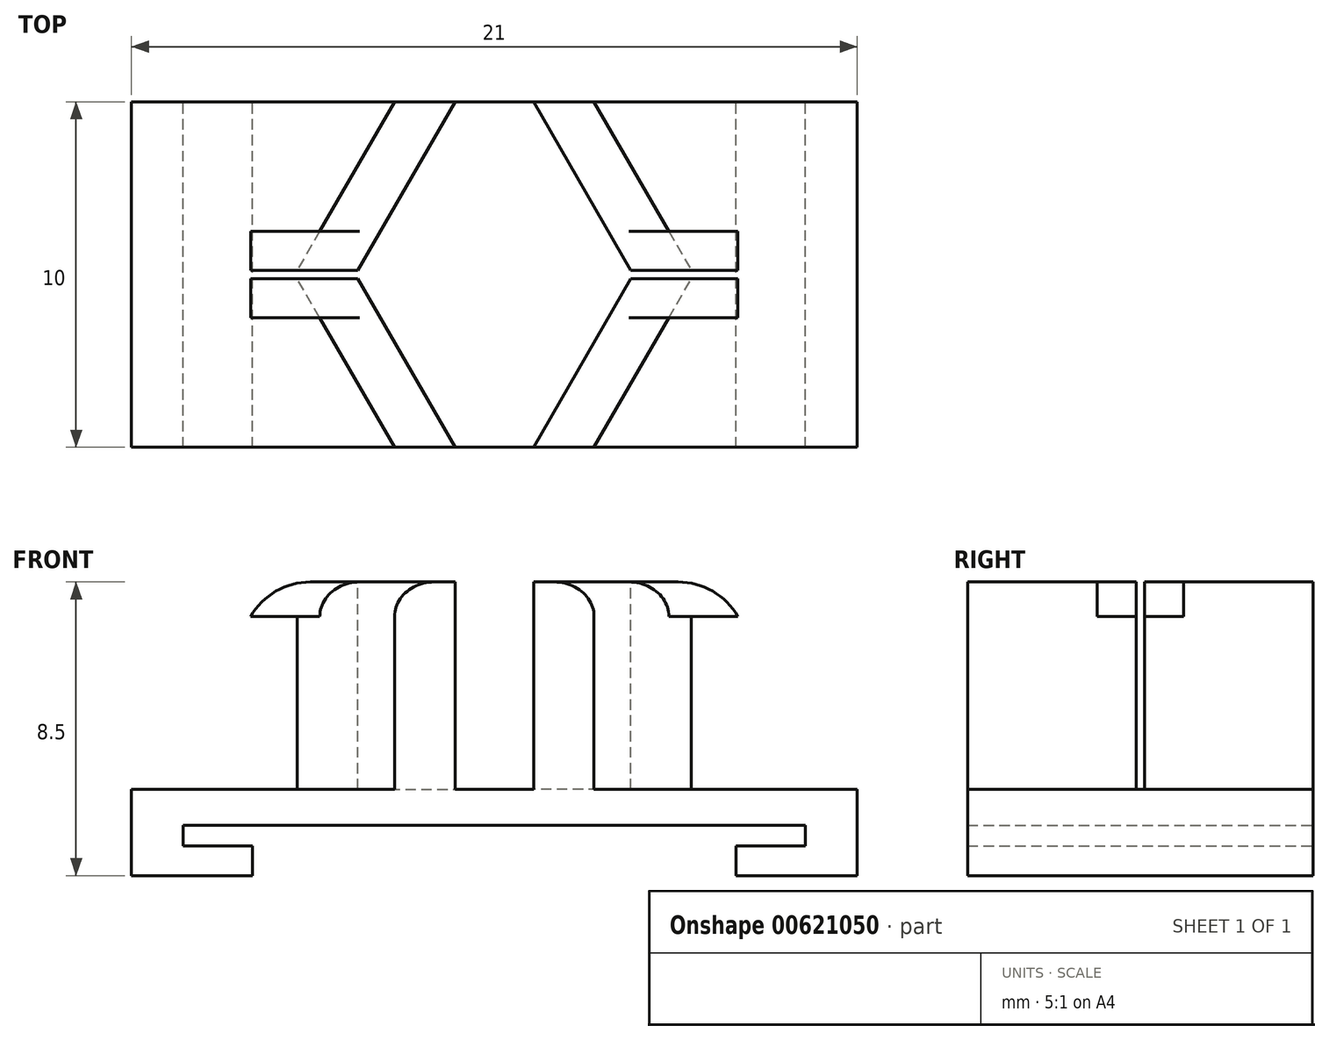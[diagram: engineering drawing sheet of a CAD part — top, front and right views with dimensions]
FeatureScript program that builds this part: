
annotation { "Feature Type Name" : "Feature", "Feature Type Description" : "" }
export const myFeature = defineFeature(function(context is Context, id is Id, definition is map)
    precondition{}
    {
        {
            var Q0;
            Q0=qCreatedBy(makeId("Front.planeOp"),FACE);
            var sketch = newSketch(context, id + "F0", { "sketchPlane" : qUnion([Q0])});
            skLineSegment(sketch, "E0.bottom", {"start": v(10.5, -1.25) * mm, "end": v(-10.5, -1.25) * mm});
            skLineSegment(sketch, "E0.top", {"start": v(10.5, 1.25) * mm, "end": v(-10.5, 1.25) * mm});
            skLineSegment(sketch, "E0.left", {"start": v(10.5, -1.25) * mm, "end": v(10.5, 1.25) * mm});
            skLineSegment(sketch, "E0.right", {"start": v(-10.5, -1.25) * mm, "end": v(-10.5, 1.25) * mm});
            skPoint(sketch, "E0.middle", {"position": v(0, 0) * mm});
            skLineSegment(sketch, "E1", {"start": v(-7, -1.25) * mm, "end": v(-7, -0.4) * mm});
            skLineSegment(sketch, "E2", {"start": v(-7, -0.4) * mm, "end": v(-9, -0.4) * mm});
            skLineSegment(sketch, "E3", {"start": v(-9, -0.4) * mm, "end": v(-9, 0.2) * mm});
            skLineSegment(sketch, "E4", {"start": v(-9, 0.2) * mm, "end": v(9, 0.2) * mm});
            skLineSegment(sketch, "E5", {"start": v(9, 0.2) * mm, "end": v(9, -0.4) * mm});
            skLineSegment(sketch, "E6", {"start": v(9, -0.4) * mm, "end": v(7, -0.4) * mm});
            skLineSegment(sketch, "E7", {"start": v(7, -0.4) * mm, "end": v(7, -1.25) * mm});
            skSolve(sketch);
        }
        {
            var Q0;
            Q0=makeQuery(id+"F0.imprint","IMPRINT",FACE,{"disambiguationData":[TD([[makeQuery(id+"F0.imprint","IMPRINT",EDGE,{"derivedFrom":sQuery(id+"F0.wireOp",EDGE,"E0.top")}),1.0]])]});
            extrude(context, id + "F1", {"entities" : qUnion([Q0]), "depth" : 10 * mm, "offsetDistance" : 25 * mm});
        }
        {
            var Q0;
            Q0=makeQuery(id+"F1.opExtrude","SWEPT_FACE",FACE,{"disambiguationData":[OSD([sQuery(id+"F0.wireOp",EDGE,"E0.top")])]});
            var sketch = newSketch(context, id + "F2", { "sketchPlane" : qUnion([Q0])});
            skLineSegment(sketch, "E8", {"start": v(0, 0) * mm, "end": v(0, -10) * mm});
            skLineSegment(sketch, "E9", {"start": v(-10.5, -5) * mm, "end": v(10.5, -5) * mm});
            skLineSegment(sketch, "E10", {"start": v(5.77, -5) * mm, "end": v(-5.77, -5) * mm});
            skPoint(sketch, "E11", {"position": v(0, -5) * mm});
            skLineSegment(sketch, "E12", {"start": v(2.89, 0) * mm, "end": v(-2.89, 0) * mm});
            skLineSegment(sketch, "E13", {"start": v(2.89, -10) * mm, "end": v(-2.89, -10) * mm});
            skLineSegment(sketch, "E14", {"start": v(2.89, 0) * mm, "end": v(5.77, -5) * mm});
            skLineSegment(sketch, "E15", {"start": v(2.89, -10) * mm, "end": v(5.77, -5) * mm});
            skLineSegment(sketch, "E16", {"start": v(-2.89, 0) * mm, "end": v(-5.77, -5) * mm});
            skLineSegment(sketch, "E17", {"start": v(-2.89, -10) * mm, "end": v(-5.77, -5) * mm});
            skLineSegment(sketch, "E18", {"start": v(-1.14, 0) * mm, "end": v(-4.02, -5) * mm});
            skLineSegment(sketch, "E19", {"start": v(-4.02, -5) * mm, "end": v(-1.14, -10) * mm});
            skLineSegment(sketch, "E20", {"start": v(1.14, 0) * mm, "end": v(4.02, -5) * mm});
            skLineSegment(sketch, "E21", {"start": v(4.02, -5) * mm, "end": v(1.14, -10) * mm});
            skSolve(sketch);
        }
        {
            var Q0;
            {var subQ6=sQuery(id+"F2.wireOp",EDGE,"E19");Q0=makeQuery(id+"F2.imprint","IMPRINT",FACE,{"disambiguationData":[TD([[makeQuery(id+"F2.imprint","IMPRINT",EDGE,{"derivedFrom":subQ6}),-1.0]])]});}
            var Q1;
            {var subQ6=sQuery(id+"F2.wireOp",EDGE,"E18");Q1=makeQuery(id+"F2.imprint","IMPRINT",FACE,{"disambiguationData":[TD([[makeQuery(id+"F2.imprint","IMPRINT",EDGE,{"derivedFrom":subQ6}),-1.0]])]});}
            var Q2;
            {var subQ6=sQuery(id+"F2.wireOp",EDGE,"E20");Q2=makeQuery(id+"F2.imprint","IMPRINT",FACE,{"disambiguationData":[TD([[makeQuery(id+"F2.imprint","IMPRINT",EDGE,{"derivedFrom":subQ6}),1.0]])]});}
            var Q3;
            {var subQ4=sQuery(id+"F2.wireOp",EDGE,"E21");Q3=makeQuery(id+"F2.imprint","IMPRINT",FACE,{"disambiguationData":[TD([[makeQuery(id+"F2.imprint","IMPRINT",EDGE,{"derivedFrom":subQ4}),1.0]])]});}
            extrude(context, id + "F3", {"entities" : qUnion([Q0, Q1, Q2, Q3]), "operationType" : NewBodyOperationType.ADD, "depth" : 6 * mm, "offsetDistance" : 25 * mm});
        }
        {
            var Q0;
            Q0=makeQuery(id+"F3.opExtrude","CAP_FACE",FACE,{"disambiguationData":[OSD([sQuery(id+"F2.wireOp",EDGE,"E12"),sQuery(id+"F2.wireOp",EDGE,"E13"),sQuery(id+"F2.wireOp",EDGE,"E16"),sQuery(id+"F2.wireOp",EDGE,"E17"),sQuery(id+"F2.wireOp",EDGE,"E18"),sQuery(id+"F2.wireOp",EDGE,"E19")])],"isStart":false});
            var sketch = newSketch(context, id + "F4", { "sketchPlane" : qUnion([Q0])});
            skLineSegment(sketch, "E22", {"start": v(-5.05, -3.75) * mm, "end": v(-7.05, -3.75) * mm});
            skLineSegment(sketch, "E23", {"start": v(-7.05, -3.75) * mm, "end": v(-7.05, -6.25) * mm});
            skLineSegment(sketch, "E24", {"start": v(-7.05, -6.25) * mm, "end": v(-5.05, -6.25) * mm});
            skSolve(sketch);
        }
        {
            var Q0;
            Q0=makeQuery(id+"F3.opExtrude","CAP_FACE",FACE,{"disambiguationData":[OSD([sQuery(id+"F2.wireOp",EDGE,"E12"),sQuery(id+"F2.wireOp",EDGE,"E13"),sQuery(id+"F2.wireOp",EDGE,"E14"),sQuery(id+"F2.wireOp",EDGE,"E15"),sQuery(id+"F2.wireOp",EDGE,"E20"),sQuery(id+"F2.wireOp",EDGE,"E21")])],"isStart":false});
            var sketch = newSketch(context, id + "F5", { "sketchPlane" : qUnion([Q0])});
            skLineSegment(sketch, "E25", {"start": v(5.05, -3.75) * mm, "end": v(7.05, -3.75) * mm});
            skLineSegment(sketch, "E26", {"start": v(7.05, -3.75) * mm, "end": v(7.05, -6.25) * mm});
            skLineSegment(sketch, "E27", {"start": v(7.05, -6.25) * mm, "end": v(5.05, -6.25) * mm});
            skSolve(sketch);
        }
        {
            var Q0;
            Q0 = qSketchRegion(id + "F4", true);
            var Q1;
            {var subQ3=sQuery(id+"F4.wireOp",EDGE,"E22");Q1=makeQuery(id+"F4.imprint","IMPRINT",FACE,{"disambiguationData":[TD([[makeQuery(id+"F4.imprint","IMPRINT",EDGE,{"derivedFrom":subQ3}),1.0]])]});}
            extrude(context, id + "F6", {"entities" : qUnion([Q0, Q1]), "operationType" : NewBodyOperationType.ADD, "oppositeDirection" : true, "depth" : 1 * mm, "offsetDistance" : 25 * mm});
        }
        {
            var Q0;
            Q0 = qSketchRegion(id + "F5", true);
            var Q1;
            {var subQ3=sQuery(id+"F5.wireOp",EDGE,"E25");Q1=makeQuery(id+"F5.imprint","IMPRINT",FACE,{"disambiguationData":[TD([[makeQuery(id+"F5.imprint","IMPRINT",EDGE,{"derivedFrom":subQ3}),-1.0]])]});}
            extrude(context, id + "F7", {"entities" : qUnion([Q0, Q1]), "operationType" : NewBodyOperationType.ADD, "oppositeDirection" : true, "depth" : 1 * mm, "offsetDistance" : 25 * mm});
        }
        {
            var Q0;
            Q0=makeQuery(id+"F6.opExtrude","CAP_EDGE",EDGE,{"disambiguationData":[OSD([sQuery(id+"F4.wireOp",EDGE,"E23")])],"isStart":true});
            var Q1;
            Q1=makeQuery(id+"F7.opExtrude","CAP_EDGE",EDGE,{"disambiguationData":[OSD([sQuery(id+"F5.wireOp",EDGE,"E26")])],"isStart":true});
            fillet(context, id + "F8", {"entities" : qUnion([Q0, Q1]), "radius" : 2 * mm, "tangentPropagation" : true, "allowEdgeOverflow" : false});
        }
        {
            var Q0;
            Q0=makeQuery(id+"F3.opExtrude","CAP_EDGE",EDGE,{"disambiguationData":[OSD([sQuery(id+"F2.wireOp",EDGE,"E17")])],"isStart":false});
            var Q1;
            Q1=makeQuery(id+"F3.opExtrude","CAP_EDGE",EDGE,{"disambiguationData":[OSD([sQuery(id+"F2.wireOp",EDGE,"E16")])],"isStart":false});
            var Q2;
            Q2=makeQuery(id+"F3.opExtrude","CAP_EDGE",EDGE,{"disambiguationData":[OSD([sQuery(id+"F2.wireOp",EDGE,"E15")])],"isStart":false});
            var Q3;
            Q3=makeQuery(id+"F3.opExtrude","CAP_EDGE",EDGE,{"disambiguationData":[OSD([sQuery(id+"F2.wireOp",EDGE,"E14")])],"isStart":false});
            fillet(context, id + "F9", {"entities" : qUnion([Q0, Q1, Q2, Q3]), "radius" : 1 * mm, "tangentPropagation" : true, "allowEdgeOverflow" : false});
        }
        {
            var Q0;
            {var subQ0=sQuery(id+"F2.wireOp",EDGE,"E17");var subQ1=sQuery(id+"F2.wireOp",EDGE,"E16");Q0=makeQuery(id+"F6.boolean.opBoolean","MERGE",FACE,{"derivedFrom":[makeQuery(id+"F3.opExtrude","CAP_FACE",FACE,{"disambiguationData":[OSD([sQuery(id+"F2.wireOp",EDGE,"E12"),sQuery(id+"F2.wireOp",EDGE,"E13"),subQ1,subQ0,sQuery(id+"F2.wireOp",EDGE,"E18"),sQuery(id+"F2.wireOp",EDGE,"E19")])],"isStart":false}),makeQuery(id+"F6.opExtrude","CAP_FACE",FACE,{"disambiguationData":[OSD([subQ1,subQ0,sQuery(id+"F4.wireOp",EDGE,"E22"),sQuery(id+"F4.wireOp",EDGE,"E23"),sQuery(id+"F4.wireOp",EDGE,"E24")])],"isStart":true})]});}
            var sketch = newSketch(context, id + "F10", { "sketchPlane" : qUnion([Q0])});
            skLineSegment(sketch, "E28.bottom", {"start": v(-3.95, -4.87) * mm, "end": v(-8.95, -4.88) * mm});
            skLineSegment(sketch, "E28.top", {"start": v(-3.95, -5.12) * mm, "end": v(-8.95, -5.12) * mm});
            skLineSegment(sketch, "E28.left", {"start": v(-3.95, -4.87) * mm, "end": v(-3.95, -5.12) * mm});
            skLineSegment(sketch, "E28.right", {"start": v(-8.95, -4.88) * mm, "end": v(-8.95, -5.12) * mm});
            skSolve(sketch);
        }
        {
            var Q0;
            {var subQ0=sQuery(id+"F2.wireOp",EDGE,"E19");var subQ1=makeQuery(id+"F3.opExtrude","CAP_EDGE",EDGE,{"disambiguationData":[OSD([subQ0])],"isStart":false});var subQ2=sQuery(id+"F2.wireOp",EDGE,"E18");var subQ3=makeQuery(id+"F3.opExtrude","CAP_EDGE",EDGE,{"disambiguationData":[OSD([subQ2])],"isStart":false});var subQ4=makeQuery(id+"F10.imprint","INTERSECT",VERTEX,{"derivedFrom":[subQ3,subQ1]});Q0=makeQuery(id+"F10.imprint","IMPRINT",FACE,{"disambiguationData":[TD([[makeQuery(id+"F10.imprint","IMPRINT",EDGE,{"disambiguationData":[TD([[subQ4,1.0]])],"derivedFrom":subQ3}),-1.0]])]});}
            var Q1;
            {var subQ0=sQuery(id+"F10.wireOp",EDGE,"E28.right");Q1=makeQuery(id+"F10.imprint","IMPRINT",FACE,{"disambiguationData":[TD([[makeQuery(id+"F10.imprint","IMPRINT",EDGE,{"derivedFrom":subQ0}),1.0]])]});}
            extrude(context, id + "F11", {"entities" : qUnion([Q0, Q1]), "operationType" : NewBodyOperationType.REMOVE, "oppositeDirection" : true, "depth" : 6 * mm, "offsetDistance" : 25 * mm});
        }
        {
            var Q0;
            {var subQ0=sQuery(id+"F2.wireOp",EDGE,"E15");var subQ1=sQuery(id+"F2.wireOp",EDGE,"E14");Q0=makeQuery(id+"F7.boolean.opBoolean","MERGE",FACE,{"derivedFrom":[makeQuery(id+"F3.opExtrude","CAP_FACE",FACE,{"disambiguationData":[OSD([sQuery(id+"F2.wireOp",EDGE,"E12"),sQuery(id+"F2.wireOp",EDGE,"E13"),subQ1,subQ0,sQuery(id+"F2.wireOp",EDGE,"E20"),sQuery(id+"F2.wireOp",EDGE,"E21")])],"isStart":false}),makeQuery(id+"F7.opExtrude","CAP_FACE",FACE,{"disambiguationData":[OSD([subQ1,subQ0,sQuery(id+"F5.wireOp",EDGE,"E25"),sQuery(id+"F5.wireOp",EDGE,"E26"),sQuery(id+"F5.wireOp",EDGE,"E27")])],"isStart":true})]});}
            var sketch = newSketch(context, id + "F12", { "sketchPlane" : qUnion([Q0])});
            skLineSegment(sketch, "E29.bottom", {"start": v(3.95, -4.87) * mm, "end": v(8.95, -4.87) * mm});
            skLineSegment(sketch, "E29.top", {"start": v(3.95, -5.12) * mm, "end": v(8.95, -5.12) * mm});
            skLineSegment(sketch, "E29.left", {"start": v(3.95, -4.87) * mm, "end": v(3.95, -5.12) * mm});
            skLineSegment(sketch, "E29.right", {"start": v(8.95, -4.87) * mm, "end": v(8.95, -5.12) * mm});
            skSolve(sketch);
        }
        {
            var Q0;
            {var subQ0=sQuery(id+"F12.wireOp",EDGE,"E29.right");Q0=makeQuery(id+"F12.imprint","IMPRINT",FACE,{"disambiguationData":[TD([[makeQuery(id+"F12.imprint","IMPRINT",EDGE,{"derivedFrom":subQ0}),-1.0]])]});}
            var Q1;
            {var subQ0=sQuery(id+"F2.wireOp",EDGE,"E21");var subQ1=makeQuery(id+"F3.opExtrude","CAP_EDGE",EDGE,{"disambiguationData":[OSD([subQ0])],"isStart":false});var subQ2=sQuery(id+"F2.wireOp",EDGE,"E20");var subQ3=makeQuery(id+"F3.opExtrude","CAP_EDGE",EDGE,{"disambiguationData":[OSD([subQ2])],"isStart":false});var subQ4=makeQuery(id+"F12.imprint","INTERSECT",VERTEX,{"derivedFrom":[subQ3,subQ1]});Q1=makeQuery(id+"F12.imprint","IMPRINT",FACE,{"disambiguationData":[TD([[makeQuery(id+"F12.imprint","IMPRINT",EDGE,{"disambiguationData":[TD([[subQ4,1.0]])],"derivedFrom":subQ3}),1.0]])]});}
            extrude(context, id + "F13", {"entities" : qUnion([Q0, Q1]), "operationType" : NewBodyOperationType.REMOVE, "oppositeDirection" : true, "depth" : 6 * mm, "offsetDistance" : 25 * mm});
        }
    });
